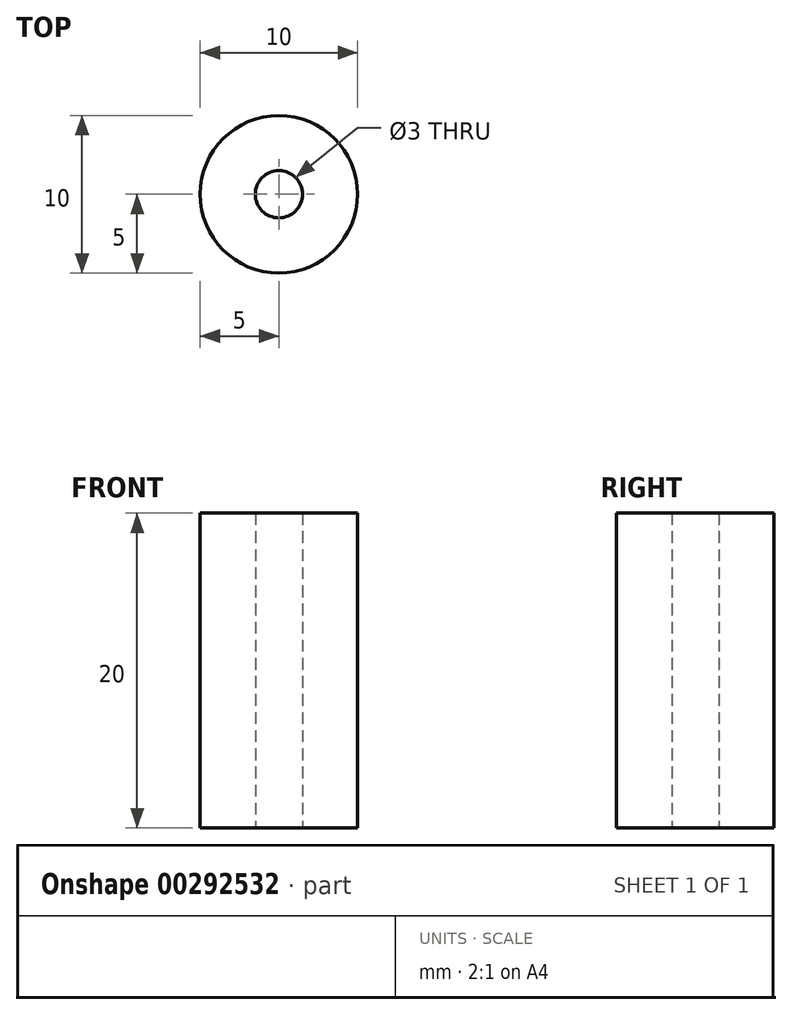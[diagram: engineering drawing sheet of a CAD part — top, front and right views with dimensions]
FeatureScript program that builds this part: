
annotation { "Feature Type Name" : "Feature", "Feature Type Description" : "" }
export const myFeature = defineFeature(function(context is Context, id is Id, definition is map)
    precondition{}
    {
        {
            var Q0;
            Q0=qCreatedBy(makeId("Top.planeOp"),FACE);
            var sketch = newSketch(context, id + "F0", { "sketchPlane" : qUnion([Q0])});
            skCircle(sketch, "E0", {"center": v(0, 0) * mm, "radius": 1.5 * mm});
            skCircle(sketch, "E1", {"center": v(0, 0) * mm, "radius": 5 * mm});
            skSolve(sketch);
        }
        {
            var Q0;
            Q0=makeQuery(id+"F0.imprint","IMPRINT",FACE,{"disambiguationData":[TD([[makeQuery(id+"F0.imprint","IMPRINT",EDGE,{"derivedFrom":sQuery(id+"F0.wireOp",EDGE,"E0")}),-1.0]])]});
            extrude(context, id + "F1", {"entities" : qUnion([Q0]), "depth" : 20 * mm, "offsetDistance" : 25 * mm});
        }
    });
